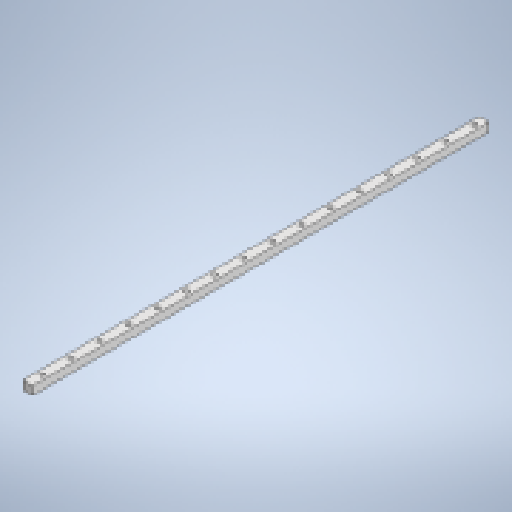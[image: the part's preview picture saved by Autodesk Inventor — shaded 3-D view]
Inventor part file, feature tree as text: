
AUTODESK INVENTOR PART (.ipt)
format: ipt  version: 2023 (Build 270158000, 158)  size: 178,688 bytes
history: native  units: mm
features: extrude x3, sketch x3, pattern_linear x1
ambient origin geometry x8: Origin, YZ Plane, XZ Plane, XY Plane, X Axis, Y Axis, Z Axis, Center Point
bodies: Solid1 (feature_tree)
feature tree (7):
  extrude  "Extrusion1"  Depth=17.5mm
  extrude  "Extrusion2"  Depth=950.0mm
  extrude  "Extrusion3"  Depth=8.5mm TaperAngle=0.0deg
  pattern_linear  "Rectangular Pattern1"  Spacing1=9.5mm  [1 undecoded]
  sketch  "Sketch1"  dims[d0=20.0mm d1=17.5mm]
  sketch  "Sketch2"  dims[d2=950.0mm d3=0.0mm d4=6.0mm]
  sketch  "Sketch3"  dims[d5=20.0mm d6=800.0mm d7=0.0mm d8=9.5mm d9=8.5mm d10=0.0mm d11=180.0mm d13=60.0mm]
note: 1 required parameter value undecoded (feature->parameter linkage not recoverable at this tier; creation-order binding heuristic only, values carry confidence <= 0.55)
